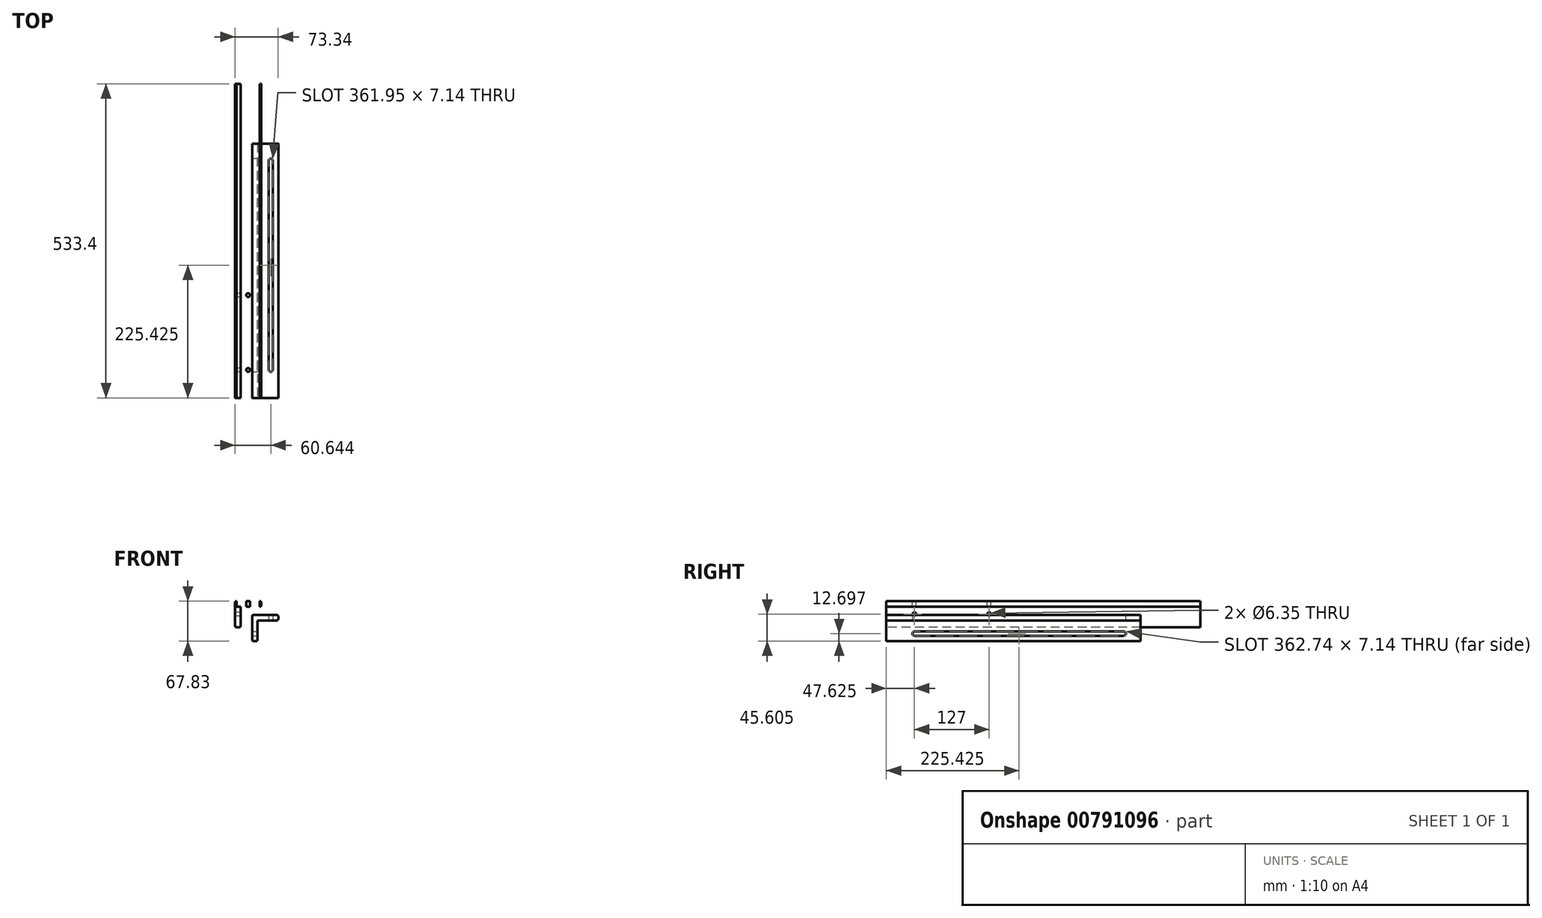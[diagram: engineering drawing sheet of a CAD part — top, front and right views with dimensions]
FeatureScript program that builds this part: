
annotation { "Feature Type Name" : "Feature", "Feature Type Description" : "" }
export const myFeature = defineFeature(function(context is Context, id is Id, definition is map)
    precondition{}
    {
        {
            var Q0;
            Q0=qCreatedBy(makeId("Front.planeOp"),FACE);
            var sketch = newSketch(context, id + "F0", { "sketchPlane" : qUnion([Q0])});
            skLineSegment(sketch, "E0", {"start": v(0, -41.91) * mm, "end": v(0, -2.54) * mm});
            skLineSegment(sketch, "E1", {"start": v(2.54, 0) * mm, "end": v(41.91, 0) * mm});
            skLineSegment(sketch, "E2", {"start": v(44.45, -2.54) * mm, "end": v(44.45, -6.99) * mm});
            skLineSegment(sketch, "E3", {"start": v(41.91, -9.53) * mm, "end": v(9.52, -9.53) * mm});
            skLineSegment(sketch, "E4", {"start": v(9.52, -9.53) * mm, "end": v(9.53, -41.91) * mm});
            skLineSegment(sketch, "E5", {"start": v(6.99, -44.45) * mm, "end": v(2.54, -44.45) * mm});
            skPoint(sketch, "E6.visualSharp", {"position": v(0, -44.45) * mm});
            skArc(sketch, "E6.filletArc", {"start": v(0, -41.91) * mm, "mid": v(0.74, -43.7) * mm, "end": v(2.54, -44.45) * mm});
            skPoint(sketch, "E7.visualSharp", {"position": v(44.45, 0) * mm});
            skArc(sketch, "E7.filletArc", {"start": v(44.45, -2.54) * mm, "mid": v(43.7, -0.74) * mm, "end": v(41.91, 0) * mm});
            skPoint(sketch, "E8.visualSharp", {"position": v(44.45, -9.53) * mm});
            skArc(sketch, "E8.filletArc", {"start": v(41.91, -9.53) * mm, "mid": v(43.7, -8.78) * mm, "end": v(44.45, -6.99) * mm});
            skPoint(sketch, "E9.visualSharp", {"position": v(9.53, -44.45) * mm});
            skArc(sketch, "E9.filletArc", {"start": v(6.99, -44.45) * mm, "mid": v(8.78, -43.7) * mm, "end": v(9.53, -41.91) * mm});
            skPoint(sketch, "E10.visualSharp", {"position": v(0, 0) * mm});
            skArc(sketch, "E10.filletArc", {"start": v(2.54, 0) * mm, "mid": v(0.74, -0.74) * mm, "end": v(0, -2.54) * mm});
            skSolve(sketch);
        }
        {
            var Q0;
            Q0=qCreatedBy(makeId("Front.planeOp"),FACE);
            var sketch = newSketch(context, id + "F1", { "sketchPlane" : qUnion([Q0])});
            skLineSegment(sketch, "E11", {"start": v(28.9, -65.3) * mm, "end": v(28.9, -25.92) * mm});
            skLineSegment(sketch, "E12", {"start": v(31.43, -23.38) * mm, "end": v(70.8, -23.38) * mm});
            skLineSegment(sketch, "E13", {"start": v(73.34, -25.92) * mm, "end": v(73.34, -30.37) * mm});
            skLineSegment(sketch, "E14", {"start": v(70.8, -32.9) * mm, "end": v(38.42, -32.9) * mm});
            skLineSegment(sketch, "E15", {"start": v(38.42, -32.9) * mm, "end": v(38.42, -65.3) * mm});
            skLineSegment(sketch, "E16", {"start": v(35.88, -67.83) * mm, "end": v(31.43, -67.83) * mm});
            skPoint(sketch, "E17.visualSharp", {"position": v(28.9, -67.83) * mm});
            skArc(sketch, "E17.filletArc", {"start": v(28.9, -65.3) * mm, "mid": v(29.64, -67.09) * mm, "end": v(31.43, -67.83) * mm});
            skPoint(sketch, "E18.visualSharp", {"position": v(73.34, -23.38) * mm});
            skArc(sketch, "E18.filletArc", {"start": v(73.34, -25.92) * mm, "mid": v(72.6, -24.13) * mm, "end": v(70.8, -23.38) * mm});
            skPoint(sketch, "E19.visualSharp", {"position": v(73.34, -32.9) * mm});
            skArc(sketch, "E19.filletArc", {"start": v(70.8, -32.9) * mm, "mid": v(72.6, -32.16) * mm, "end": v(73.34, -30.37) * mm});
            skPoint(sketch, "E20.visualSharp", {"position": v(38.42, -67.83) * mm});
            skArc(sketch, "E20.filletArc", {"start": v(35.88, -67.83) * mm, "mid": v(37.68, -67.09) * mm, "end": v(38.42, -65.3) * mm});
            skPoint(sketch, "E21.visualSharp", {"position": v(28.9, -23.38) * mm});
            skArc(sketch, "E21.filletArc", {"start": v(31.43, -23.38) * mm, "mid": v(29.64, -24.13) * mm, "end": v(28.9, -25.92) * mm});
            skSolve(sketch);
        }
        {
            var Q0;
            Q0 = qSketchRegion(id + "F0", true);
            extrude(context, id + "F2", {"entities" : qUnion([Q0]), "oppositeDirection" : true, "depth" : 533.4 * mm, "offsetDistance" : 25.4 * mm});
        }
        {
            var Q0;
            Q0 = qSketchRegion(id + "F1", true);
            extrude(context, id + "F3", {"entities" : qUnion([Q0]), "oppositeDirection" : true, "depth" : 431.8 * mm, "offsetDistance" : 25.4 * mm});
        }
        {
            var Q0;
            Q0=makeQuery(id+"F3.opExtrude","SWEPT_FACE",FACE,{"disambiguationData":[OSD([sQuery(id+"F1.wireOp",EDGE,"E14")])]});
            var sketch = newSketch(context, id + "F4", { "sketchPlane" : qUnion([Q0])});
            skCircle(sketch, "E22", {"center": v(60.64, -48.02) * mm, "radius": 3.57 * mm});
            skCircle(sketch, "E23", {"center": v(60.64, -402.83) * mm, "radius": 3.57 * mm});
            skLineSegment(sketch, "E24", {"start": v(60.64, 0) * mm, "end": v(60.64, -431.8) * mm});
            skLineSegment(sketch, "E25", {"start": v(57.07, -48.02) * mm, "end": v(57.07, -402.83) * mm});
            skLineSegment(sketch, "E26", {"start": v(64.22, -402.83) * mm, "end": v(64.22, -48.02) * mm});
            skLineSegment(sketch, "E27", {"start": v(38.42, 0) * mm, "end": v(60.64, 0) * mm});
            skSolve(sketch);
        }
        {
            var Q0;
            Q0 = qSketchRegion(id + "F4", true);
            var Q1;
            Q1=makeQuery(id+"F3.opExtrude","SWEPT_FACE",FACE,{"disambiguationData":[OSD([sQuery(id+"F1.wireOp",EDGE,"E12")])]});
            extrude(context, id + "F5", {"entities" : qUnion([Q0]), "operationType" : NewBodyOperationType.REMOVE, "endBound" : BoundingType.UP_TO_SURFACE, "oppositeDirection" : true, "depth" : 12.7 * mm, "endBoundEntityFace" : qUnion([Q1]), "offsetDistance" : 25.4 * mm});
        }
        {
            var Q0;
            Q0=makeQuery(id+"F3.opExtrude","SWEPT_FACE",FACE,{"disambiguationData":[OSD([sQuery(id+"F1.wireOp",EDGE,"E15")])]});
            var sketch = newSketch(context, id + "F6", { "sketchPlane" : qUnion([Q0])});
            skCircle(sketch, "E28", {"center": v(47.63, -55.13) * mm, "radius": 3.57 * mm});
            skCircle(sketch, "E29", {"center": v(403.23, -55.13) * mm, "radius": 3.57 * mm});
            skLineSegment(sketch, "E30", {"start": v(47.62, -58.7) * mm, "end": v(403.23, -58.7) * mm});
            skLineSegment(sketch, "E31", {"start": v(403.23, -51.56) * mm, "end": v(47.62, -51.56) * mm});
            skLineSegment(sketch, "E32", {"start": v(0, -65.3) * mm, "end": v(0, -32.9) * mm});
            skLineSegment(sketch, "E33", {"start": v(0, -55.13) * mm, "end": v(47.63, -55.13) * mm});
            skLineSegment(sketch, "E34", {"start": v(403.23, -55.13) * mm, "end": v(431.8, -55.13) * mm});
            skSolve(sketch);
        }
        {
            var Q0;
            Q0 = qSketchRegion(id + "F6", true);
            var Q1;
            Q1=makeQuery(id+"F3.opExtrude","SWEPT_FACE",FACE,{"disambiguationData":[OSD([sQuery(id+"F1.wireOp",EDGE,"E11")])]});
            extrude(context, id + "F7", {"entities" : qUnion([Q0]), "operationType" : NewBodyOperationType.REMOVE, "endBound" : BoundingType.UP_TO_SURFACE, "oppositeDirection" : true, "depth" : 25.4 * mm, "endBoundEntityFace" : qUnion([Q1]), "offsetDistance" : 25.4 * mm});
        }
        {
            var Q0;
            Q0=makeQuery(id+"F2.opExtrude","SWEPT_FACE",FACE,{"disambiguationData":[OSD([sQuery(id+"F0.wireOp",EDGE,"E0")])]});
            var sketch = newSketch(context, id + "F8", { "sketchPlane" : qUnion([Q0])});
            skLineSegment(sketch, "E35", {"start": v(0, -22.23) * mm, "end": v(-533.4, -22.23) * mm});
            skLineSegment(sketch, "E36", {"start": v(0, -22.23) * mm, "end": v(-47.62, -22.23) * mm});
            skCircle(sketch, "E37", {"center": v(-47.62, -22.23) * mm, "radius": 3.18 * mm});
            skLineSegment(sketch, "E38", {"start": v(-47.62, -22.23) * mm, "end": v(-174.62, -22.23) * mm});
            skCircle(sketch, "E39", {"center": v(-174.62, -22.23) * mm, "radius": 3.18 * mm});
            skSolve(sketch);
        }
        {
            var Q0;
            Q0 = qSketchRegion(id + "F8", true);
            var Q1;
            Q1=makeQuery(id+"F2.opExtrude","SWEPT_FACE",FACE,{"disambiguationData":[OSD([sQuery(id+"F0.wireOp",EDGE,"E4")])]});
            extrude(context, id + "F9", {"entities" : qUnion([Q0]), "operationType" : NewBodyOperationType.REMOVE, "endBound" : BoundingType.UP_TO_SURFACE, "oppositeDirection" : true, "depth" : 25.4 * mm, "endBoundEntityFace" : qUnion([Q1]), "offsetDistance" : 25.4 * mm});
        }
        {
            var Q0;
            Q0 = qSketchRegion(id + "F8", true);
            var Q1;
            Q1=makeQuery(id+"F2.opExtrude","SWEPT_FACE",FACE,{"disambiguationData":[OSD([sQuery(id+"F0.wireOp",EDGE,"E4")])]});
            extrude(context, id + "F10", {"entities" : qUnion([Q0]), "operationType" : NewBodyOperationType.REMOVE, "endBound" : BoundingType.UP_TO_SURFACE, "oppositeDirection" : true, "depth" : 25.4 * mm, "endBoundEntityFace" : qUnion([Q1]), "offsetDistance" : 25.4 * mm});
        }
        {
            var Q0;
            Q0=makeQuery(id+"F2.opExtrude","SWEPT_FACE",FACE,{"disambiguationData":[OSD([sQuery(id+"F0.wireOp",EDGE,"E1")])]});
            var sketch = newSketch(context, id + "F11", { "sketchPlane" : qUnion([Q0])});
            skLineSegment(sketch, "E40", {"start": v(22.23, 0) * mm, "end": v(22.23, 533.4) * mm});
            skLineSegment(sketch, "E41", {"start": v(22.23, 0) * mm, "end": v(22.23, 47.62) * mm});
            skCircle(sketch, "E42", {"center": v(22.23, 47.62) * mm, "radius": 3.18 * mm});
            skLineSegment(sketch, "E43", {"start": v(22.23, 47.62) * mm, "end": v(22.23, 174.62) * mm});
            skCircle(sketch, "E44", {"center": v(22.23, 174.62) * mm, "radius": 3.18 * mm});
            skSolve(sketch);
        }
        {
            var Q0;
            {var subQ0=sQuery(id+"F11.wireOp",EDGE,"E43");var subQ1=sQuery(id+"F11.wireOp",EDGE,"E41");var subQ2=makeQuery(id+"F11.imprint","INTERSECT",VERTEX,{"derivedFrom":[subQ1,subQ0]});Q0=makeQuery(id+"F11.imprint","IMPRINT",FACE,{"disambiguationData":[TD([[makeQuery(id+"F11.imprint","IMPRINT",EDGE,{"disambiguationData":[TD([[subQ2,1.0]])],"derivedFrom":subQ1}),-1.0]])]});}
            var Q1;
            {var subQ0=sQuery(id+"F11.wireOp",EDGE,"E43");var subQ1=sQuery(id+"F11.wireOp",EDGE,"E41");var subQ2=makeQuery(id+"F11.imprint","INTERSECT",VERTEX,{"derivedFrom":[subQ1,subQ0]});Q1=makeQuery(id+"F11.imprint","IMPRINT",FACE,{"disambiguationData":[TD([[makeQuery(id+"F11.imprint","IMPRINT",EDGE,{"disambiguationData":[TD([[subQ2,1.0]])],"derivedFrom":subQ1}),1.0]])]});}
            var Q2;
            {var subQ0=sQuery(id+"F11.wireOp",EDGE,"E43");var subQ1=sQuery(id+"F11.wireOp",EDGE,"E40");var subQ2=makeQuery(id+"F11.imprint","INTERSECT",VERTEX,{"derivedFrom":[subQ1,subQ0]});Q2=makeQuery(id+"F11.imprint","IMPRINT",FACE,{"disambiguationData":[TD([[makeQuery(id+"F11.imprint","IMPRINT",EDGE,{"disambiguationData":[TD([[subQ2,-1.0]])],"derivedFrom":subQ1}),-1.0]])]});}
            var Q3;
            {var subQ0=sQuery(id+"F11.wireOp",EDGE,"E43");var subQ1=sQuery(id+"F11.wireOp",EDGE,"E40");var subQ2=makeQuery(id+"F11.imprint","INTERSECT",VERTEX,{"derivedFrom":[subQ1,subQ0]});Q3=makeQuery(id+"F11.imprint","IMPRINT",FACE,{"disambiguationData":[TD([[makeQuery(id+"F11.imprint","IMPRINT",EDGE,{"disambiguationData":[TD([[subQ2,-1.0]])],"derivedFrom":subQ1}),1.0]])]});}
            var Q4;
            Q4=makeQuery(id+"F2.opExtrude","SWEPT_FACE",FACE,{"disambiguationData":[OSD([sQuery(id+"F0.wireOp",EDGE,"E3")])]});
            extrude(context, id + "F12", {"entities" : qUnion([Q0, Q1, Q2, Q3]), "operationType" : NewBodyOperationType.REMOVE, "endBound" : BoundingType.UP_TO_SURFACE, "oppositeDirection" : true, "depth" : 25.4 * mm, "endBoundEntityFace" : qUnion([Q4]), "offsetDistance" : 25.4 * mm});
        }
    });
